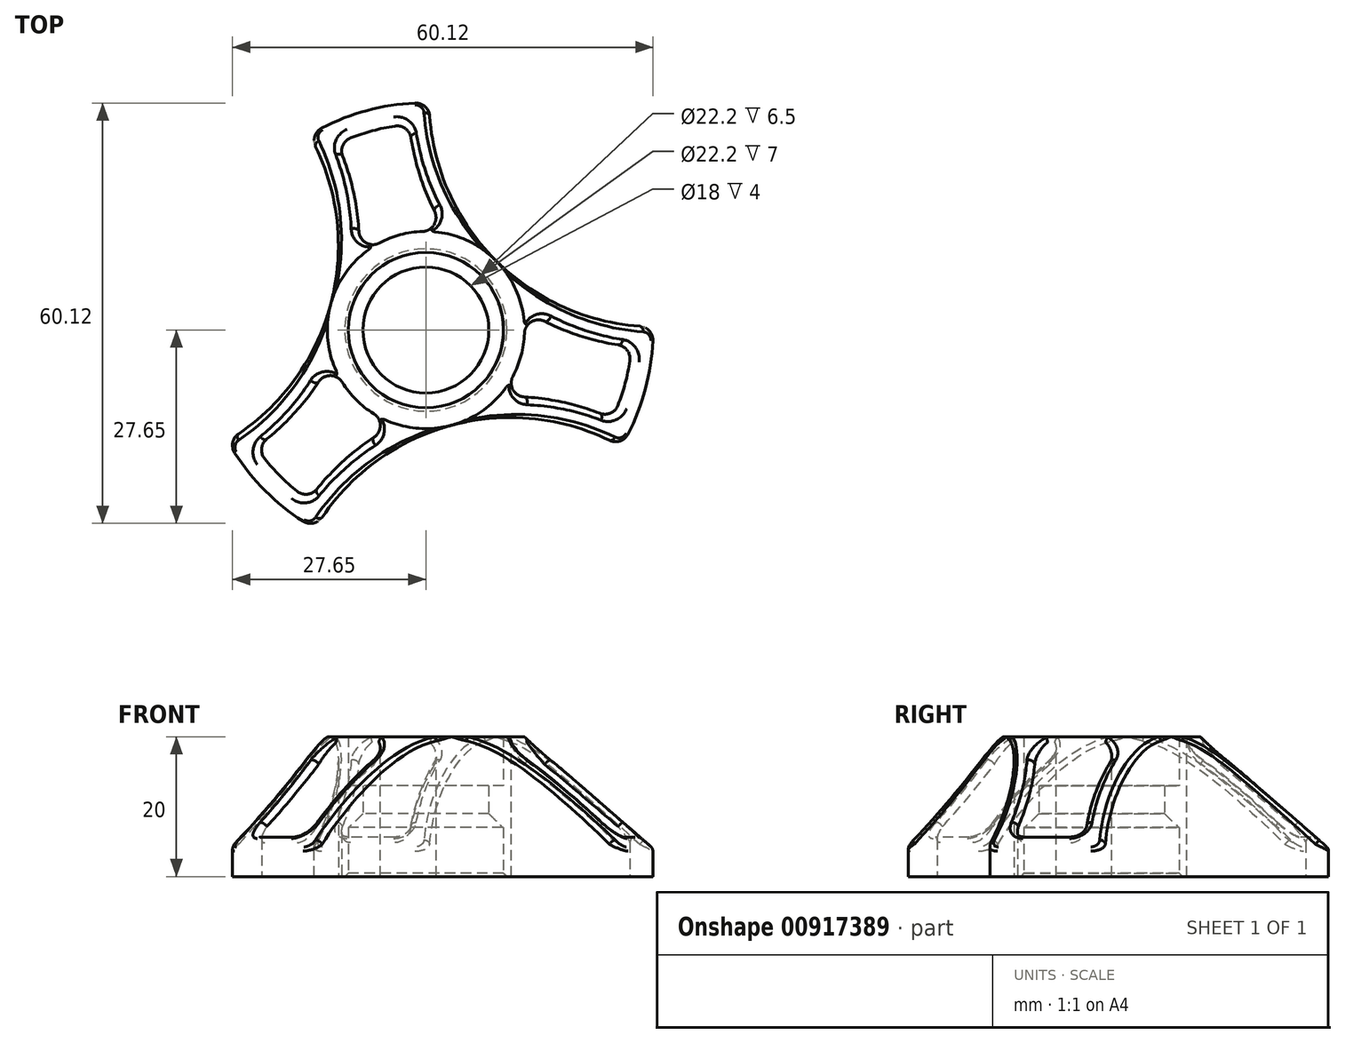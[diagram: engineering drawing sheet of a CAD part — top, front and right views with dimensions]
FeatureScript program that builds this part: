
annotation { "Feature Type Name" : "Feature", "Feature Type Description" : "" }
export const myFeature = defineFeature(function(context is Context, id is Id, definition is map)
    precondition{}
    {
        {
            assignVariable(context, id + "F0", {"name" : "height", "anyValue" : 20});
        }
        {
            var Q0;
            Q0=qCreatedBy(makeId("Top.planeOp"),FACE);
            var sketch = newSketch(context, id + "F1", { "sketchPlane" : qUnion([Q0])});
            skCircle(sketch, "E0", {"center": v(0, 0) * mm, "radius": 32.5 * mm});
            skCircle(sketch, "E1", {"center": v(0, 0) * mm, "radius": 11.1 * mm});
            skCircle(sketch, "E2", {"center": v(0, 0) * mm, "radius": 9 * mm});
            skLineSegment(sketch, "E3", {"start": v(0, 0) * mm, "end": v(56.5, 56.5) * mm, "construction": true});
            skCircle(sketch, "E4", {"center": v(32.95, 32.95) * mm, "radius": 32.5 * mm});
            skCircle(sketch, "E5", {"center": v(0, 0) * mm, "radius": 14.1 * mm, "construction": true});
            skCircle(sketch, "E6.1.0", {"center": v(-45.01, 12.06) * mm, "radius": 32.5 * mm});
            skCircle(sketch, "E6.2.0", {"center": v(12.06, -45.01) * mm, "radius": 32.5 * mm});
            skSolve(sketch);
        }
        {
            var Q0;
            Q0=makeQuery(id+"F1.imprint","IMPRINT",FACE,{"disambiguationData":[TD([[makeQuery(id+"F1.imprint","IMPRINT",EDGE,{"derivedFrom":sQuery(id+"F1.wireOp",EDGE,"E5")}),-1.0]])]});
            var Q1;
            Q1=makeQuery(id+"F1.imprint","IMPRINT",FACE,{"disambiguationData":[TD([[makeQuery(id+"F1.imprint","IMPRINT",EDGE,{"derivedFrom":sQuery(id+"F1.wireOp",EDGE,"E1")}),-1.0]])]});
            extrude(context, id + "F2", {"entities" : qUnion([Q0, Q1]), "depth" : (getVariable(context, 'height')) * mm, "offsetDistance" : 25 * mm});
        }
        {
            var Q0;
            Q0=makeQuery(id+"F2.opExtrude","CAP_FACE",FACE,{"disambiguationData":[OSD([sQuery(id+"F1.wireOp",EDGE,"E0"),sQuery(id+"F1.wireOp",EDGE,"E1"),sQuery(id+"F1.wireOp",EDGE,"E4"),sQuery(id+"F1.wireOp",EDGE,"E6.1.0"),sQuery(id+"F1.wireOp",EDGE,"E6.2.0")])],"isStart":false});
            shell(context, id + "F3", {"entities" : qUnion([Q0]), "thickness" : 3 * mm});
        }
        {
            var Q0;
            Q0=makeQuery(id+"F3.opShell","OFFSET_FACE",FACE,{"disambiguationData":[OSD([sQuery(id+"F1.wireOp",EDGE,"E0"),sQuery(id+"F1.wireOp",EDGE,"E1"),sQuery(id+"F1.wireOp",EDGE,"E4"),sQuery(id+"F1.wireOp",EDGE,"E6.1.0"),sQuery(id+"F1.wireOp",EDGE,"E6.2.0")]),OD(2.0)]});
            var Q1;
            Q1=makeQuery(id+"F3.opShell","OFFSET_FACE",FACE,{"disambiguationData":[OSD([sQuery(id+"F1.wireOp",EDGE,"E0"),sQuery(id+"F1.wireOp",EDGE,"E1"),sQuery(id+"F1.wireOp",EDGE,"E4"),sQuery(id+"F1.wireOp",EDGE,"E6.1.0"),sQuery(id+"F1.wireOp",EDGE,"E6.2.0")]),OD(0.0)]});
            var Q2;
            Q2=makeQuery(id+"F3.opShell","OFFSET_FACE",FACE,{"disambiguationData":[OSD([sQuery(id+"F1.wireOp",EDGE,"E0"),sQuery(id+"F1.wireOp",EDGE,"E1"),sQuery(id+"F1.wireOp",EDGE,"E4"),sQuery(id+"F1.wireOp",EDGE,"E6.1.0"),sQuery(id+"F1.wireOp",EDGE,"E6.2.0")]),OD(1.0)]});
            extrude(context, id + "F4", {"entities" : qUnion([Q0, Q1, Q2]), "operationType" : NewBodyOperationType.REMOVE, "endBound" : BoundingType.THROUGH_ALL, "oppositeDirection" : true, "depth" : 25 * mm, "offsetDistance" : 25 * mm});
        }
        {
            var Q0;
            Q0=makeQuery(id+"F1.imprint","IMPRINT",FACE,{"disambiguationData":[TD([[makeQuery(id+"F1.imprint","IMPRINT",EDGE,{"derivedFrom":sQuery(id+"F1.wireOp",EDGE,"E1")}),1.0]])]});
            extrude(context, id + "F5", {"entities" : qUnion([Q0]), "operationType" : NewBodyOperationType.ADD, "depth" : (getVariable(context, 'height') - 7) * mm, "offsetDistance" : 25 * mm, "hasSecondDirection" : true, "secondDirectionOppositeDirection" : false, "secondDirectionDepth" : 7 * mm});
        }
        {
            var Q0;
            Q0=makeQuery(id+"F5.opExtrude","CAP_EDGE",EDGE,{"disambiguationData":[OSD([sQuery(id+"F1.wireOp",EDGE,"E2")])],"isStart":true});
            chamfer(context, id + "F6", {"entities" : qUnion([Q0]), "width" : 2 * mm, "tangentPropagation" : true});
        }
        {
            var Q0;
            {var subQ0=sQuery(id+"F1.wireOp",EDGE,"E0");Q0=makeQuery(id+"F2.opExtrude","CAP_EDGE",EDGE,{"disambiguationData":[OSD([subQ0]),TDD([makeQuery(id+"F1.imprint","IMPRINT",EDGE,{"disambiguationData":[TD([[makeQuery(id+"F1.imprint","INTERSECT",VERTEX,{"disambiguationData":[OD(1.0)],"derivedFrom":[subQ0,sQuery(id+"F1.wireOp",EDGE,"E6.1.0")]}),-1.0]])],"derivedFrom":subQ0})])],"isStart":false});}
            var Q1;
            {var subQ0=sQuery(id+"F1.wireOp",EDGE,"E0");Q1=makeQuery(id+"F2.opExtrude","CAP_EDGE",EDGE,{"disambiguationData":[OSD([subQ0]),TDD([makeQuery(id+"F1.imprint","IMPRINT",EDGE,{"disambiguationData":[TD([[makeQuery(id+"F1.imprint","INTERSECT",VERTEX,{"disambiguationData":[OD(0.0)],"derivedFrom":[subQ0,sQuery(id+"F1.wireOp",EDGE,"E4")]}),-1.0]])],"derivedFrom":subQ0})])],"isStart":false});}
            var Q2;
            {var subQ0=sQuery(id+"F1.wireOp",EDGE,"E0");Q2=makeQuery(id+"F2.opExtrude","CAP_EDGE",EDGE,{"disambiguationData":[OSD([subQ0]),TDD([makeQuery(id+"F1.imprint","IMPRINT",EDGE,{"disambiguationData":[TD([[makeQuery(id+"F1.imprint","INTERSECT",VERTEX,{"disambiguationData":[OD(1.0)],"derivedFrom":[subQ0,sQuery(id+"F1.wireOp",EDGE,"E4")]}),1.0]])],"derivedFrom":subQ0})])],"isStart":false});}
            chamfer(context, id + "F7", {"entities" : qUnion([Q0, Q1, Q2]), "chamferType" : ChamferType.TWO_OFFSETS, "width1" : 18.4 * mm, "oppositeDirection" : false, "width2" : (getVariable(context, 'height') - 4) * mm, "tangentPropagation" : true});
        }
        {
            var Q0;
            {var subQ0=sQuery(id+"F1.wireOp",EDGE,"E6.2.0");var subQ1=sQuery(id+"F1.wireOp",EDGE,"E0");Q0=makeQuery(id+"F2.opExtrude","SWEPT_EDGE",EDGE,{"disambiguationData":[OSD([subQ1,subQ0]),TDD([makeQuery(id+"F1.imprint","INTERSECT",VERTEX,{"disambiguationData":[OD(1.0)],"derivedFrom":[subQ1,subQ0]})])]});}
            var Q1;
            {var subQ0=sQuery(id+"F1.wireOp",EDGE,"E6.2.0");var subQ1=sQuery(id+"F1.wireOp",EDGE,"E0");var subQ2=makeQuery(id+"F1.imprint","INTERSECT",VERTEX,{"disambiguationData":[OD(1.0)],"derivedFrom":[subQ1,subQ0]});Q1=makeQuery(id+"F4.boolean.opBoolean","MERGE",EDGE,{"derivedFrom":[makeQuery(id+"F3.opShell","OFFSET_EDGE",EDGE,{"disambiguationData":[OSD([subQ1,subQ0]),TDD([makeQuery(id+"F2.opExtrude","SWEPT_EDGE",EDGE,{"disambiguationData":[OSD([subQ1,subQ0]),TDD([subQ2])]})])]})],"fromTools":[makeQuery(id+"F4.opExtrude","SWEPT_EDGE",EDGE,{"disambiguationData":[OSD([subQ1,subQ0]),TDD([makeQuery(id+"F3.opShell","OFFSET_VERTEX",VERTEX,{"disambiguationData":[OSD([subQ1,subQ0]),TDD([makeQuery(id+"F2.opExtrude","CAP_VERTEX",VERTEX,{"disambiguationData":[OSD([subQ1,subQ0]),TDD([subQ2])],"isStart":true})])]})])]})]});}
            var Q2;
            {var subQ0=sQuery(id+"F1.wireOp",EDGE,"E4");var subQ1=sQuery(id+"F1.wireOp",EDGE,"E0");Q2=makeQuery(id+"F2.opExtrude","SWEPT_EDGE",EDGE,{"disambiguationData":[OSD([subQ1,subQ0]),TDD([makeQuery(id+"F1.imprint","INTERSECT",VERTEX,{"disambiguationData":[OD(1.0)],"derivedFrom":[subQ1,subQ0]})])]});}
            var Q3;
            {var subQ0=sQuery(id+"F1.wireOp",EDGE,"E4");var subQ1=sQuery(id+"F1.wireOp",EDGE,"E0");Q3=makeQuery(id+"F2.opExtrude","SWEPT_EDGE",EDGE,{"disambiguationData":[OSD([subQ1,subQ0]),TDD([makeQuery(id+"F1.imprint","INTERSECT",VERTEX,{"disambiguationData":[OD(0.0)],"derivedFrom":[subQ1,subQ0]})])]});}
            var Q4;
            {var subQ0=sQuery(id+"F1.wireOp",EDGE,"E6.1.0");var subQ1=sQuery(id+"F1.wireOp",EDGE,"E0");Q4=makeQuery(id+"F2.opExtrude","SWEPT_EDGE",EDGE,{"disambiguationData":[OSD([subQ1,subQ0]),TDD([makeQuery(id+"F1.imprint","INTERSECT",VERTEX,{"disambiguationData":[OD(0.0)],"derivedFrom":[subQ1,subQ0]})])]});}
            var Q5;
            {var subQ0=sQuery(id+"F1.wireOp",EDGE,"E6.1.0");var subQ1=sQuery(id+"F1.wireOp",EDGE,"E0");Q5=makeQuery(id+"F2.opExtrude","SWEPT_EDGE",EDGE,{"disambiguationData":[OSD([subQ1,subQ0]),TDD([makeQuery(id+"F1.imprint","INTERSECT",VERTEX,{"disambiguationData":[OD(1.0)],"derivedFrom":[subQ1,subQ0]})])]});}
            var Q6;
            {var subQ0=sQuery(id+"F1.wireOp",EDGE,"E6.2.0");var subQ1=sQuery(id+"F1.wireOp",EDGE,"E0");Q6=makeQuery(id+"F2.opExtrude","SWEPT_EDGE",EDGE,{"disambiguationData":[OSD([subQ1,subQ0]),TDD([makeQuery(id+"F1.imprint","INTERSECT",VERTEX,{"disambiguationData":[OD(0.0)],"derivedFrom":[subQ1,subQ0]})])]});}
            var Q7;
            {var subQ0=sQuery(id+"F1.wireOp",EDGE,"E4");var subQ1=sQuery(id+"F1.wireOp",EDGE,"E0");var subQ2=makeQuery(id+"F1.imprint","INTERSECT",VERTEX,{"disambiguationData":[OD(0.0)],"derivedFrom":[subQ1,subQ0]});Q7=makeQuery(id+"F4.boolean.opBoolean","MERGE",EDGE,{"derivedFrom":[makeQuery(id+"F3.opShell","OFFSET_EDGE",EDGE,{"disambiguationData":[OSD([subQ1,subQ0]),TDD([makeQuery(id+"F2.opExtrude","SWEPT_EDGE",EDGE,{"disambiguationData":[OSD([subQ1,subQ0]),TDD([subQ2])]})])]})],"fromTools":[makeQuery(id+"F4.opExtrude","SWEPT_EDGE",EDGE,{"disambiguationData":[OSD([subQ1,subQ0]),TDD([makeQuery(id+"F3.opShell","OFFSET_VERTEX",VERTEX,{"disambiguationData":[OSD([subQ1,subQ0]),TDD([makeQuery(id+"F2.opExtrude","CAP_VERTEX",VERTEX,{"disambiguationData":[OSD([subQ1,subQ0]),TDD([subQ2])],"isStart":true})])]})])]})]});}
            var Q8;
            {var subQ0=sQuery(id+"F1.wireOp",EDGE,"E4");var subQ1=sQuery(id+"F1.wireOp",EDGE,"E0");var subQ2=makeQuery(id+"F1.imprint","INTERSECT",VERTEX,{"disambiguationData":[OD(1.0)],"derivedFrom":[subQ1,subQ0]});Q8=makeQuery(id+"F4.boolean.opBoolean","MERGE",EDGE,{"derivedFrom":[makeQuery(id+"F3.opShell","OFFSET_EDGE",EDGE,{"disambiguationData":[OSD([subQ1,subQ0]),TDD([makeQuery(id+"F2.opExtrude","SWEPT_EDGE",EDGE,{"disambiguationData":[OSD([subQ1,subQ0]),TDD([subQ2])]})])]})],"fromTools":[makeQuery(id+"F4.opExtrude","SWEPT_EDGE",EDGE,{"disambiguationData":[OSD([subQ1,subQ0]),TDD([makeQuery(id+"F3.opShell","OFFSET_VERTEX",VERTEX,{"disambiguationData":[OSD([subQ1,subQ0]),TDD([makeQuery(id+"F2.opExtrude","CAP_VERTEX",VERTEX,{"disambiguationData":[OSD([subQ1,subQ0]),TDD([subQ2])],"isStart":true})])]})])]})]});}
            var Q9;
            {var subQ0=sQuery(id+"F1.wireOp",EDGE,"E6.2.0");var subQ1=sQuery(id+"F1.wireOp",EDGE,"E0");var subQ2=makeQuery(id+"F1.imprint","INTERSECT",VERTEX,{"disambiguationData":[OD(0.0)],"derivedFrom":[subQ1,subQ0]});Q9=makeQuery(id+"F4.boolean.opBoolean","MERGE",EDGE,{"derivedFrom":[makeQuery(id+"F3.opShell","OFFSET_EDGE",EDGE,{"disambiguationData":[OSD([subQ1,subQ0]),TDD([makeQuery(id+"F2.opExtrude","SWEPT_EDGE",EDGE,{"disambiguationData":[OSD([subQ1,subQ0]),TDD([subQ2])]})])]})],"fromTools":[makeQuery(id+"F4.opExtrude","SWEPT_EDGE",EDGE,{"disambiguationData":[OSD([subQ1,subQ0]),TDD([makeQuery(id+"F3.opShell","OFFSET_VERTEX",VERTEX,{"disambiguationData":[OSD([subQ1,subQ0]),TDD([makeQuery(id+"F2.opExtrude","CAP_VERTEX",VERTEX,{"disambiguationData":[OSD([subQ1,subQ0]),TDD([subQ2])],"isStart":true})])]})])]})]});}
            var Q10;
            {var subQ0=sQuery(id+"F1.wireOp",EDGE,"E6.1.0");var subQ1=sQuery(id+"F1.wireOp",EDGE,"E0");var subQ2=makeQuery(id+"F1.imprint","INTERSECT",VERTEX,{"disambiguationData":[OD(1.0)],"derivedFrom":[subQ1,subQ0]});Q10=makeQuery(id+"F4.boolean.opBoolean","MERGE",EDGE,{"derivedFrom":[makeQuery(id+"F3.opShell","OFFSET_EDGE",EDGE,{"disambiguationData":[OSD([subQ1,subQ0]),TDD([makeQuery(id+"F2.opExtrude","SWEPT_EDGE",EDGE,{"disambiguationData":[OSD([subQ1,subQ0]),TDD([subQ2])]})])]})],"fromTools":[makeQuery(id+"F4.opExtrude","SWEPT_EDGE",EDGE,{"disambiguationData":[OSD([subQ1,subQ0]),TDD([makeQuery(id+"F3.opShell","OFFSET_VERTEX",VERTEX,{"disambiguationData":[OSD([subQ1,subQ0]),TDD([makeQuery(id+"F2.opExtrude","CAP_VERTEX",VERTEX,{"disambiguationData":[OSD([subQ1,subQ0]),TDD([subQ2])],"isStart":true})])]})])]})]});}
            var Q11;
            {var subQ0=sQuery(id+"F1.wireOp",EDGE,"E6.1.0");var subQ1=sQuery(id+"F1.wireOp",EDGE,"E0");var subQ2=makeQuery(id+"F1.imprint","INTERSECT",VERTEX,{"disambiguationData":[OD(0.0)],"derivedFrom":[subQ1,subQ0]});Q11=makeQuery(id+"F4.boolean.opBoolean","MERGE",EDGE,{"derivedFrom":[makeQuery(id+"F3.opShell","OFFSET_EDGE",EDGE,{"disambiguationData":[OSD([subQ1,subQ0]),TDD([makeQuery(id+"F2.opExtrude","SWEPT_EDGE",EDGE,{"disambiguationData":[OSD([subQ1,subQ0]),TDD([subQ2])]})])]})],"fromTools":[makeQuery(id+"F4.opExtrude","SWEPT_EDGE",EDGE,{"disambiguationData":[OSD([subQ1,subQ0]),TDD([makeQuery(id+"F3.opShell","OFFSET_VERTEX",VERTEX,{"disambiguationData":[OSD([subQ1,subQ0]),TDD([makeQuery(id+"F2.opExtrude","CAP_VERTEX",VERTEX,{"disambiguationData":[OSD([subQ1,subQ0]),TDD([subQ2])],"isStart":true})])]})])]})]});}
            var Q12;
            {var subQ0=sQuery(id+"F1.wireOp",EDGE,"E4");var subQ1=makeQuery(id+"F2.opExtrude","SWEPT_FACE",FACE,{"disambiguationData":[OSD([subQ0])]});var subQ2=sQuery(id+"F1.wireOp",EDGE,"E1");var subQ3=makeQuery(id+"F2.opExtrude","SWEPT_FACE",FACE,{"disambiguationData":[OSD([subQ2])]});var subQ4=sQuery(id+"F1.wireOp",EDGE,"E6.2.0");var subQ5=sQuery(id+"F1.wireOp",EDGE,"E6.1.0");var subQ6=sQuery(id+"F1.wireOp",EDGE,"E0");Q12=makeQuery(id+"F4.boolean.opBoolean","MERGE",EDGE,{"derivedFrom":[makeQuery(id+"F3.opShell","TWEAK_EDGE",EDGE,{"disambiguationData":[OD(0.0)],"derivedFrom":[subQ3,subQ1]})],"fromTools":[makeQuery(id+"F4.opExtrude","SWEPT_EDGE",EDGE,{"disambiguationData":[OSD([subQ6,subQ2,subQ0,subQ5,subQ4]),TDD([makeQuery(id+"F3.opShell","TWEAK_VERTEX",VERTEX,{"disambiguationData":[OD(0.0)],"derivedFrom":[makeQuery(id+"F2.opExtrude","CAP_FACE",FACE,{"disambiguationData":[OSD([subQ6,subQ2,subQ0,subQ5,subQ4])],"isStart":true}),subQ3,subQ1]})])]})]});}
            var Q13;
            {var subQ0=sQuery(id+"F1.wireOp",EDGE,"E6.1.0");var subQ1=makeQuery(id+"F2.opExtrude","SWEPT_FACE",FACE,{"disambiguationData":[OSD([subQ0])]});var subQ2=sQuery(id+"F1.wireOp",EDGE,"E1");var subQ3=makeQuery(id+"F2.opExtrude","SWEPT_FACE",FACE,{"disambiguationData":[OSD([subQ2])]});var subQ4=sQuery(id+"F1.wireOp",EDGE,"E6.2.0");var subQ5=sQuery(id+"F1.wireOp",EDGE,"E4");var subQ6=sQuery(id+"F1.wireOp",EDGE,"E0");Q13=makeQuery(id+"F4.boolean.opBoolean","MERGE",EDGE,{"derivedFrom":[makeQuery(id+"F3.opShell","TWEAK_EDGE",EDGE,{"disambiguationData":[OD(0.0)],"derivedFrom":[subQ3,subQ1]})],"fromTools":[makeQuery(id+"F4.opExtrude","SWEPT_EDGE",EDGE,{"disambiguationData":[OSD([subQ6,subQ2,subQ5,subQ0,subQ4]),TDD([makeQuery(id+"F3.opShell","TWEAK_VERTEX",VERTEX,{"disambiguationData":[OD(0.0)],"derivedFrom":[makeQuery(id+"F2.opExtrude","CAP_FACE",FACE,{"disambiguationData":[OSD([subQ6,subQ2,subQ5,subQ0,subQ4])],"isStart":true}),subQ3,subQ1]})])]})]});}
            var Q14;
            {var subQ0=sQuery(id+"F1.wireOp",EDGE,"E6.2.0");var subQ1=makeQuery(id+"F2.opExtrude","SWEPT_FACE",FACE,{"disambiguationData":[OSD([subQ0])]});var subQ2=sQuery(id+"F1.wireOp",EDGE,"E1");var subQ3=makeQuery(id+"F2.opExtrude","SWEPT_FACE",FACE,{"disambiguationData":[OSD([subQ2])]});var subQ4=sQuery(id+"F1.wireOp",EDGE,"E6.1.0");var subQ5=sQuery(id+"F1.wireOp",EDGE,"E4");var subQ6=sQuery(id+"F1.wireOp",EDGE,"E0");Q14=makeQuery(id+"F4.boolean.opBoolean","MERGE",EDGE,{"derivedFrom":[makeQuery(id+"F3.opShell","TWEAK_EDGE",EDGE,{"disambiguationData":[OD(0.0)],"derivedFrom":[subQ3,subQ1]})],"fromTools":[makeQuery(id+"F4.opExtrude","SWEPT_EDGE",EDGE,{"disambiguationData":[OSD([subQ6,subQ2,subQ5,subQ4,subQ0]),TDD([makeQuery(id+"F3.opShell","TWEAK_VERTEX",VERTEX,{"disambiguationData":[OD(0.0)],"derivedFrom":[makeQuery(id+"F2.opExtrude","CAP_FACE",FACE,{"disambiguationData":[OSD([subQ6,subQ2,subQ5,subQ4,subQ0])],"isStart":true}),subQ3,subQ1]})])]})]});}
            var Q15;
            {var subQ0=sQuery(id+"F1.wireOp",EDGE,"E6.1.0");var subQ1=makeQuery(id+"F2.opExtrude","SWEPT_FACE",FACE,{"disambiguationData":[OSD([subQ0])]});var subQ2=sQuery(id+"F1.wireOp",EDGE,"E1");var subQ3=makeQuery(id+"F2.opExtrude","SWEPT_FACE",FACE,{"disambiguationData":[OSD([subQ2])]});var subQ4=sQuery(id+"F1.wireOp",EDGE,"E6.2.0");var subQ5=sQuery(id+"F1.wireOp",EDGE,"E4");var subQ6=sQuery(id+"F1.wireOp",EDGE,"E0");Q15=makeQuery(id+"F4.boolean.opBoolean","MERGE",EDGE,{"derivedFrom":[makeQuery(id+"F3.opShell","TWEAK_EDGE",EDGE,{"disambiguationData":[OD(1.0)],"derivedFrom":[subQ3,subQ1]})],"fromTools":[makeQuery(id+"F4.opExtrude","SWEPT_EDGE",EDGE,{"disambiguationData":[OSD([subQ6,subQ2,subQ5,subQ0,subQ4]),TDD([makeQuery(id+"F3.opShell","TWEAK_VERTEX",VERTEX,{"disambiguationData":[OD(1.0)],"derivedFrom":[makeQuery(id+"F2.opExtrude","CAP_FACE",FACE,{"disambiguationData":[OSD([subQ6,subQ2,subQ5,subQ0,subQ4])],"isStart":true}),subQ3,subQ1]})])]})]});}
            var Q16;
            {var subQ0=sQuery(id+"F1.wireOp",EDGE,"E4");var subQ1=makeQuery(id+"F2.opExtrude","SWEPT_FACE",FACE,{"disambiguationData":[OSD([subQ0])]});var subQ2=sQuery(id+"F1.wireOp",EDGE,"E1");var subQ3=makeQuery(id+"F2.opExtrude","SWEPT_FACE",FACE,{"disambiguationData":[OSD([subQ2])]});var subQ4=sQuery(id+"F1.wireOp",EDGE,"E6.2.0");var subQ5=sQuery(id+"F1.wireOp",EDGE,"E6.1.0");var subQ6=sQuery(id+"F1.wireOp",EDGE,"E0");Q16=makeQuery(id+"F4.boolean.opBoolean","MERGE",EDGE,{"derivedFrom":[makeQuery(id+"F3.opShell","TWEAK_EDGE",EDGE,{"disambiguationData":[OD(1.0)],"derivedFrom":[subQ3,subQ1]})],"fromTools":[makeQuery(id+"F4.opExtrude","SWEPT_EDGE",EDGE,{"disambiguationData":[OSD([subQ6,subQ2,subQ0,subQ5,subQ4]),TDD([makeQuery(id+"F3.opShell","TWEAK_VERTEX",VERTEX,{"disambiguationData":[OD(1.0)],"derivedFrom":[makeQuery(id+"F2.opExtrude","CAP_FACE",FACE,{"disambiguationData":[OSD([subQ6,subQ2,subQ0,subQ5,subQ4])],"isStart":true}),subQ3,subQ1]})])]})]});}
            var Q17;
            {var subQ0=sQuery(id+"F1.wireOp",EDGE,"E6.2.0");var subQ1=makeQuery(id+"F2.opExtrude","SWEPT_FACE",FACE,{"disambiguationData":[OSD([subQ0])]});var subQ2=sQuery(id+"F1.wireOp",EDGE,"E1");var subQ3=makeQuery(id+"F2.opExtrude","SWEPT_FACE",FACE,{"disambiguationData":[OSD([subQ2])]});var subQ4=sQuery(id+"F1.wireOp",EDGE,"E6.1.0");var subQ5=sQuery(id+"F1.wireOp",EDGE,"E4");var subQ6=sQuery(id+"F1.wireOp",EDGE,"E0");Q17=makeQuery(id+"F4.boolean.opBoolean","MERGE",EDGE,{"derivedFrom":[makeQuery(id+"F3.opShell","TWEAK_EDGE",EDGE,{"disambiguationData":[OD(1.0)],"derivedFrom":[subQ3,subQ1]})],"fromTools":[makeQuery(id+"F4.opExtrude","SWEPT_EDGE",EDGE,{"disambiguationData":[OSD([subQ6,subQ2,subQ5,subQ4,subQ0]),TDD([makeQuery(id+"F3.opShell","TWEAK_VERTEX",VERTEX,{"disambiguationData":[OD(1.0)],"derivedFrom":[makeQuery(id+"F2.opExtrude","CAP_FACE",FACE,{"disambiguationData":[OSD([subQ6,subQ2,subQ5,subQ4,subQ0])],"isStart":true}),subQ3,subQ1]})])]})]});}
            fillet(context, id + "F8", {"entities" : qUnion([Q0, Q1, Q2, Q3, Q4, Q5, Q6, Q7, Q8, Q9, Q10, Q11, Q12, Q13, Q14, Q15, Q16, Q17]), "radius" : 2 * mm, "tangentPropagation" : true, "allowEdgeOverflow" : false});
        }
        {
            var Q0;
            {var subQ0=sQuery(id+"F1.wireOp",EDGE,"E4");var subQ1=sQuery(id+"F1.wireOp",EDGE,"E0");Q0=makeQuery(id+"F7.opChamfer","BLEND_EDGE",EDGE,{"blendedFrom":[makeQuery(id+"F2.opExtrude","CAP_EDGE",EDGE,{"disambiguationData":[OSD([subQ1]),TDD([makeQuery(id+"F1.imprint","IMPRINT",EDGE,{"disambiguationData":[TD([[makeQuery(id+"F1.imprint","INTERSECT",VERTEX,{"disambiguationData":[OD(1.0)],"derivedFrom":[subQ1,subQ0]}),1.0]])],"derivedFrom":subQ1})])],"isStart":false}),makeQuery(id+"F4.boolean.opBoolean","MERGE",FACE,{"derivedFrom":[makeQuery(id+"F3.opShell","OFFSET_FACE",FACE,{"disambiguationData":[OSD([subQ0]),OD(1.0)]})],"fromTools":[makeQuery(id+"F4.opExtrude","SWEPT_FACE",FACE,{"disambiguationData":[OSD([subQ0]),TDD([makeQuery(id+"F3.opShell","OFFSET_EDGE",EDGE,{"disambiguationData":[OSD([subQ0]),TDD([makeQuery(id+"F2.opExtrude","CAP_EDGE",EDGE,{"disambiguationData":[OSD([subQ0])],"isStart":true})]),OD(1.0)]})])]})]})],"blendedInto":[makeQuery(id+"F4.boolean.opBoolean","MERGE",FACE,{"derivedFrom":[makeQuery(id+"F3.opShell","OFFSET_FACE",FACE,{"disambiguationData":[OSD([subQ0]),OD(1.0)]})],"fromTools":[makeQuery(id+"F4.opExtrude","SWEPT_FACE",FACE,{"disambiguationData":[OSD([subQ0]),TDD([makeQuery(id+"F3.opShell","OFFSET_EDGE",EDGE,{"disambiguationData":[OSD([subQ0]),TDD([makeQuery(id+"F2.opExtrude","CAP_EDGE",EDGE,{"disambiguationData":[OSD([subQ0])],"isStart":true})]),OD(1.0)]})])]})]})]});}
            var Q1;
            {var subQ0=sQuery(id+"F1.wireOp",EDGE,"E6.1.0");var subQ1=sQuery(id+"F1.wireOp",EDGE,"E0");Q1=makeQuery(id+"F7.opChamfer","BLEND_EDGE",EDGE,{"blendedFrom":[makeQuery(id+"F2.opExtrude","CAP_EDGE",EDGE,{"disambiguationData":[OSD([subQ1]),TDD([makeQuery(id+"F1.imprint","IMPRINT",EDGE,{"disambiguationData":[TD([[makeQuery(id+"F1.imprint","INTERSECT",VERTEX,{"disambiguationData":[OD(1.0)],"derivedFrom":[subQ1,subQ0]}),-1.0]])],"derivedFrom":subQ1})])],"isStart":false}),makeQuery(id+"F4.boolean.opBoolean","MERGE",FACE,{"derivedFrom":[makeQuery(id+"F3.opShell","OFFSET_FACE",FACE,{"disambiguationData":[OSD([subQ0]),OD(1.0)]})],"fromTools":[makeQuery(id+"F4.opExtrude","SWEPT_FACE",FACE,{"disambiguationData":[OSD([subQ0]),TDD([makeQuery(id+"F3.opShell","OFFSET_EDGE",EDGE,{"disambiguationData":[OSD([subQ0]),TDD([makeQuery(id+"F2.opExtrude","CAP_EDGE",EDGE,{"disambiguationData":[OSD([subQ0])],"isStart":true})]),OD(1.0)]})])]})]})],"blendedInto":[makeQuery(id+"F4.boolean.opBoolean","MERGE",FACE,{"derivedFrom":[makeQuery(id+"F3.opShell","OFFSET_FACE",FACE,{"disambiguationData":[OSD([subQ0]),OD(1.0)]})],"fromTools":[makeQuery(id+"F4.opExtrude","SWEPT_FACE",FACE,{"disambiguationData":[OSD([subQ0]),TDD([makeQuery(id+"F3.opShell","OFFSET_EDGE",EDGE,{"disambiguationData":[OSD([subQ0]),TDD([makeQuery(id+"F2.opExtrude","CAP_EDGE",EDGE,{"disambiguationData":[OSD([subQ0])],"isStart":true})]),OD(1.0)]})])]})]})]});}
            var Q2;
            {var subQ0=sQuery(id+"F1.wireOp",EDGE,"E6.1.0");var subQ1=sQuery(id+"F1.wireOp",EDGE,"E0");Q2=makeQuery(id+"F7.opChamfer","BLEND_EDGE",EDGE,{"blendedFrom":[makeQuery(id+"F2.opExtrude","CAP_EDGE",EDGE,{"disambiguationData":[OSD([subQ1]),TDD([makeQuery(id+"F1.imprint","IMPRINT",EDGE,{"disambiguationData":[TD([[makeQuery(id+"F1.imprint","INTERSECT",VERTEX,{"disambiguationData":[OD(0.0)],"derivedFrom":[subQ1,sQuery(id+"F1.wireOp",EDGE,"E4")]}),-1.0]])],"derivedFrom":subQ1})])],"isStart":false}),makeQuery(id+"F4.boolean.opBoolean","MERGE",FACE,{"derivedFrom":[makeQuery(id+"F3.opShell","OFFSET_FACE",FACE,{"disambiguationData":[OSD([subQ0]),OD(0.0)]})],"fromTools":[makeQuery(id+"F4.opExtrude","SWEPT_FACE",FACE,{"disambiguationData":[OSD([subQ0]),TDD([makeQuery(id+"F3.opShell","OFFSET_EDGE",EDGE,{"disambiguationData":[OSD([subQ0]),TDD([makeQuery(id+"F2.opExtrude","CAP_EDGE",EDGE,{"disambiguationData":[OSD([subQ0])],"isStart":true})]),OD(0.0)]})])]})]})],"blendedInto":[makeQuery(id+"F4.boolean.opBoolean","MERGE",FACE,{"derivedFrom":[makeQuery(id+"F3.opShell","OFFSET_FACE",FACE,{"disambiguationData":[OSD([subQ0]),OD(0.0)]})],"fromTools":[makeQuery(id+"F4.opExtrude","SWEPT_FACE",FACE,{"disambiguationData":[OSD([subQ0]),TDD([makeQuery(id+"F3.opShell","OFFSET_EDGE",EDGE,{"disambiguationData":[OSD([subQ0]),TDD([makeQuery(id+"F2.opExtrude","CAP_EDGE",EDGE,{"disambiguationData":[OSD([subQ0])],"isStart":true})]),OD(0.0)]})])]})]})]});}
            var Q3;
            {var subQ0=sQuery(id+"F1.wireOp",EDGE,"E6.2.0");var subQ1=sQuery(id+"F1.wireOp",EDGE,"E0");Q3=makeQuery(id+"F7.opChamfer","BLEND_EDGE",EDGE,{"blendedFrom":[makeQuery(id+"F2.opExtrude","CAP_EDGE",EDGE,{"disambiguationData":[OSD([subQ1]),TDD([makeQuery(id+"F1.imprint","IMPRINT",EDGE,{"disambiguationData":[TD([[makeQuery(id+"F1.imprint","INTERSECT",VERTEX,{"disambiguationData":[OD(1.0)],"derivedFrom":[subQ1,sQuery(id+"F1.wireOp",EDGE,"E6.1.0")]}),-1.0]])],"derivedFrom":subQ1})])],"isStart":false}),makeQuery(id+"F2.opExtrude","SWEPT_FACE",FACE,{"disambiguationData":[OSD([subQ0])]})],"blendedInto":[makeQuery(id+"F2.opExtrude","SWEPT_FACE",FACE,{"disambiguationData":[OSD([subQ0])]})]});}
            var Q4;
            {var subQ0=sQuery(id+"F1.wireOp",EDGE,"E0");var subQ1=makeQuery(id+"F1.imprint","IMPRINT",EDGE,{"disambiguationData":[TD([[makeQuery(id+"F1.imprint","INTERSECT",VERTEX,{"disambiguationData":[OD(1.0)],"derivedFrom":[subQ0,sQuery(id+"F1.wireOp",EDGE,"E4")]}),1.0]])],"derivedFrom":subQ0});Q4=makeQuery(id+"F7.opChamfer","BLEND_EDGE",EDGE,{"blendedFrom":[makeQuery(id+"F2.opExtrude","CAP_EDGE",EDGE,{"disambiguationData":[OSD([subQ0]),TDD([subQ1])],"isStart":false}),makeQuery(id+"F2.opExtrude","SWEPT_FACE",FACE,{"disambiguationData":[OSD([subQ0]),TDD([subQ1])]})],"blendedInto":[makeQuery(id+"F2.opExtrude","SWEPT_FACE",FACE,{"disambiguationData":[OSD([subQ0]),TDD([subQ1])]})]});}
            var Q5;
            {var subQ0=sQuery(id+"F1.wireOp",EDGE,"E0");var subQ1=makeQuery(id+"F1.imprint","IMPRINT",EDGE,{"disambiguationData":[TD([[makeQuery(id+"F1.imprint","INTERSECT",VERTEX,{"disambiguationData":[OD(0.0)],"derivedFrom":[subQ0,sQuery(id+"F1.wireOp",EDGE,"E4")]}),-1.0]])],"derivedFrom":subQ0});Q5=makeQuery(id+"F7.opChamfer","BLEND_EDGE",EDGE,{"blendedFrom":[makeQuery(id+"F2.opExtrude","CAP_EDGE",EDGE,{"disambiguationData":[OSD([subQ0]),TDD([subQ1])],"isStart":false}),makeQuery(id+"F2.opExtrude","SWEPT_FACE",FACE,{"disambiguationData":[OSD([subQ0]),TDD([subQ1])]})],"blendedInto":[makeQuery(id+"F2.opExtrude","SWEPT_FACE",FACE,{"disambiguationData":[OSD([subQ0]),TDD([subQ1])]})]});}
            fillet(context, id + "F9", {"entities" : qUnion([Q0, Q1, Q2, Q3, Q4, Q5]), "radius" : 0.8 * mm, "tangentPropagation" : true, "allowEdgeOverflow" : false});
        }
        {
            var Q0;
            Q0=makeQuery(id+"F2.opExtrude","CAP_EDGE",EDGE,{"disambiguationData":[OSD([sQuery(id+"F1.wireOp",EDGE,"E1")])],"isStart":true});
            chamfer(context, id + "F10", {"entities" : qUnion([Q0]), "width" : 0.5 * mm, "tangentPropagation" : true});
        }
    });
